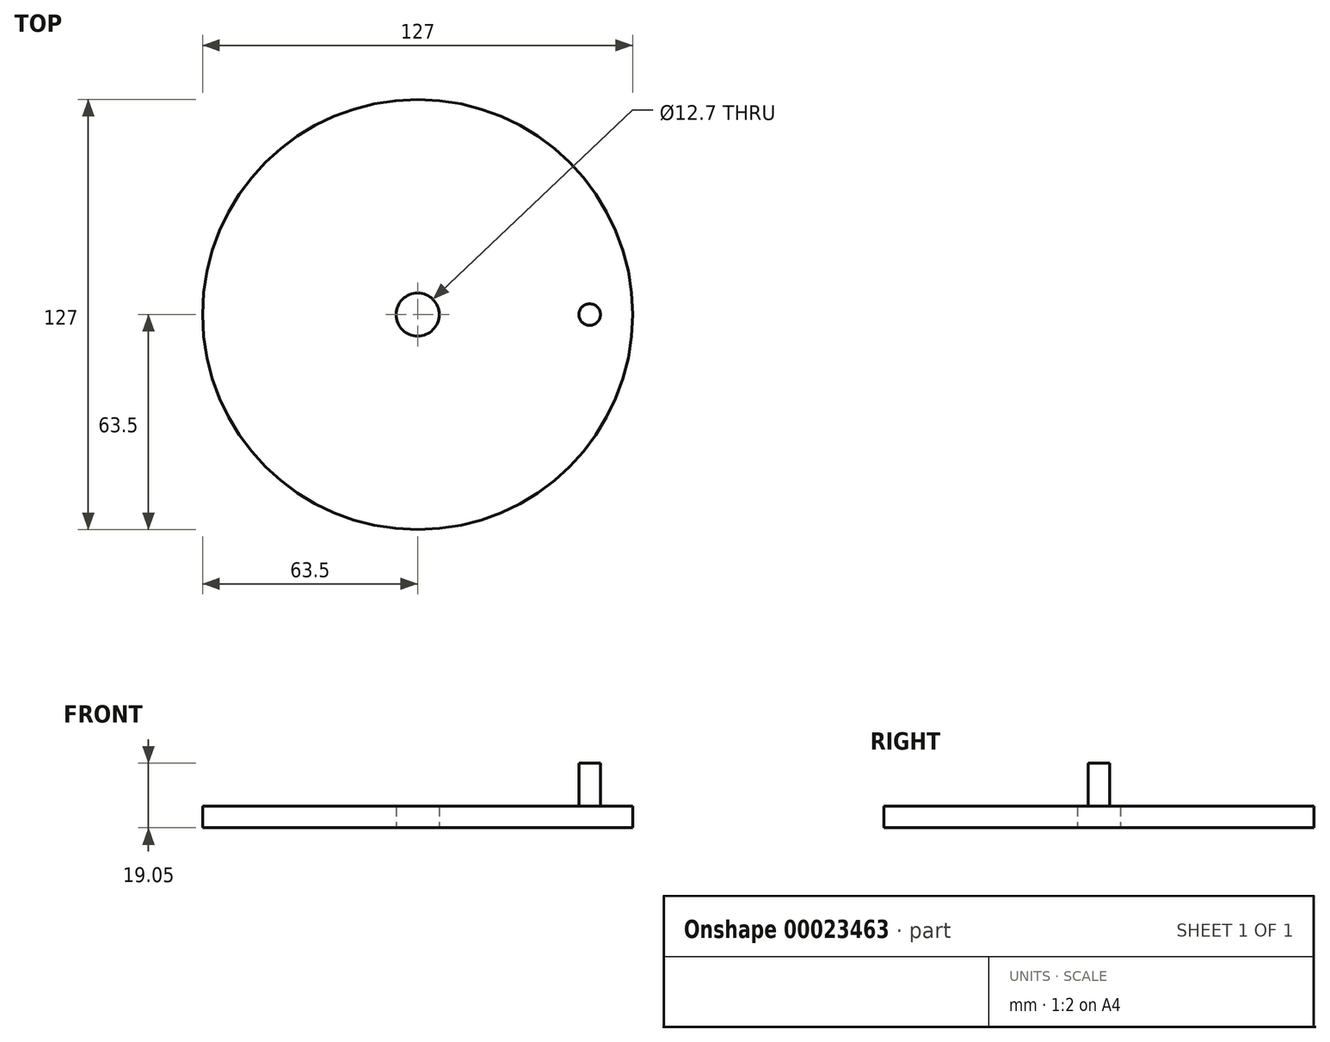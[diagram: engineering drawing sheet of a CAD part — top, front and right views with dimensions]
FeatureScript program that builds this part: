
annotation { "Feature Type Name" : "Feature", "Feature Type Description" : "" }
export const myFeature = defineFeature(function(context is Context, id is Id, definition is map)
    precondition{}
    {
        {
            var Q0;
            Q0=qCreatedBy(makeId("Top.planeOp"),FACE);
            var sketch = newSketch(context, id + "F0", { "sketchPlane" : qUnion([Q0])});
            skCircle(sketch, "E0", {"center": v(0, 0) * mm, "radius": 63.5 * mm});
            skCircle(sketch, "E1", {"center": v(50.8, 0) * mm, "radius": 3.18 * mm});
            skCircle(sketch, "E2", {"center": v(0, 0) * mm, "radius": 6.35 * mm});
            skSolve(sketch);
        }
        {
            var Q0;
            Q0 = qSketchRegion(id + "F0", true);
            var Q1;
            Q1=makeQuery(id+"F0.imprint","IMPRINT",FACE,{"disambiguationData":[TD([[makeQuery(id+"F0.imprint","IMPRINT",EDGE,{"derivedFrom":sQuery(id+"F0.wireOp",EDGE,"E1")}),1.0]])]});
            extrude(context, id + "F1", {"entities" : qUnion([Q0, Q1]), "depth" : 6.35 * mm});
        }
        {
            var Q0;
            Q0=makeQuery(id+"F0.imprint","IMPRINT",FACE,{"disambiguationData":[TD([[makeQuery(id+"F0.imprint","IMPRINT",EDGE,{"derivedFrom":sQuery(id+"F0.wireOp",EDGE,"E1")}),1.0]])]});
            extrude(context, id + "F2", {"entities" : qUnion([Q0]), "operationType" : NewBodyOperationType.ADD, "depth" : 19.05 * mm});
        }
    });
